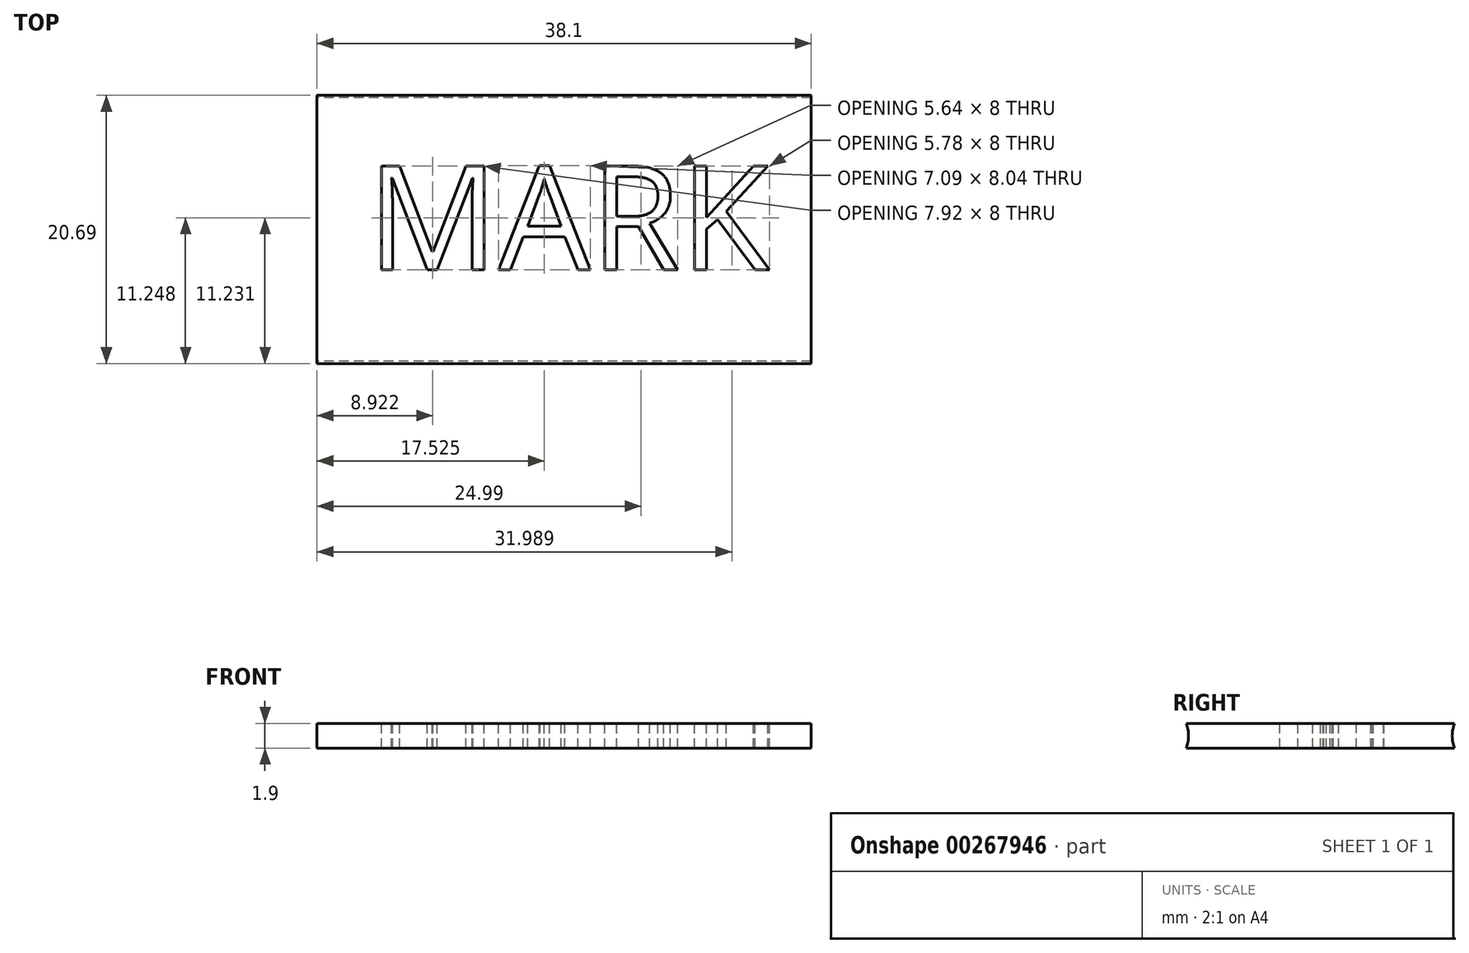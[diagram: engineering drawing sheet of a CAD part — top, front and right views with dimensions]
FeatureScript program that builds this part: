
annotation { "Feature Type Name" : "Feature", "Feature Type Description" : "" }
export const myFeature = defineFeature(function(context is Context, id is Id, definition is map)
    precondition{}
    {
        {
            var Q0;
            Q0=qCreatedBy(makeId("Right.planeOp"),FACE);
            var sketch = newSketch(context, id + "F0", { "sketchPlane" : qUnion([Q0])});
            skLineSegment(sketch, "E0", {"start": v(-13.18, 0) * mm, "end": v(12.22, 0) * mm});
            skArc(sketch, "E1", {"start": v(-10.83, -0.95) * mm, "mid": v(-10.64, 0) * mm, "end": v(-10.83, 0.95) * mm});
            skArc(sketch, "E2", {"start": v(9.86, 0.95) * mm, "mid": v(9.68, 0) * mm, "end": v(9.86, -0.95) * mm});
            skPoint(sketch, "E3", {"position": v(0, 0.95) * mm});
            skPoint(sketch, "E4", {"position": v(0, -0.95) * mm});
            skLineSegment(sketch, "E5.bottom", {"start": v(9.86, 0.95) * mm, "end": v(-10.83, 0.95) * mm});
            skLineSegment(sketch, "E5.top", {"start": v(9.86, -0.95) * mm, "end": v(-10.83, -0.95) * mm});
            skPoint(sketch, "E6.orphan", {"position": v(-13.18, 2.54) * mm});
            skPoint(sketch, "E7.orphan", {"position": v(12.22, 2.54) * mm});
            skSolve(sketch);
        }
        {
            var Q0;
            Q0 = qSketchRegion(id + "F0", true);
            extrude(context, id + "F1", {"entities" : qUnion([Q0]), "depth" : 38.1 * mm});
        }
        {
            var Q0;
            Q0=makeQuery(id+"F1.opExtrude","SWEPT_FACE",FACE,{"disambiguationData":[OSD([sQuery(id+"F0.wireOp",EDGE,"E5.bottom")])]});
            var sketch = newSketch(context, id + "F2", { "sketchPlane" : qUnion([Q0])});
            skText(sketch, "E8", { "text": "MARK", "fontName": "OpenSans-Regular.ttf"});
            const initialGuessF2  = {"E8": [0.00386, -0.0036, 1, 0, 0.00807]};
            skSetInitialGuess(sketch, initialGuessF2);
            skSolve(sketch);
        }
        {
            var Q0;
            Q0 = qSketchRegion(id + "F2", true);
            extrude(context, id + "F3", {"entities" : qUnion([Q0]), "operationType" : NewBodyOperationType.REMOVE, "oppositeDirection" : true, "depth" : 25.4 * mm});
        }
    });
